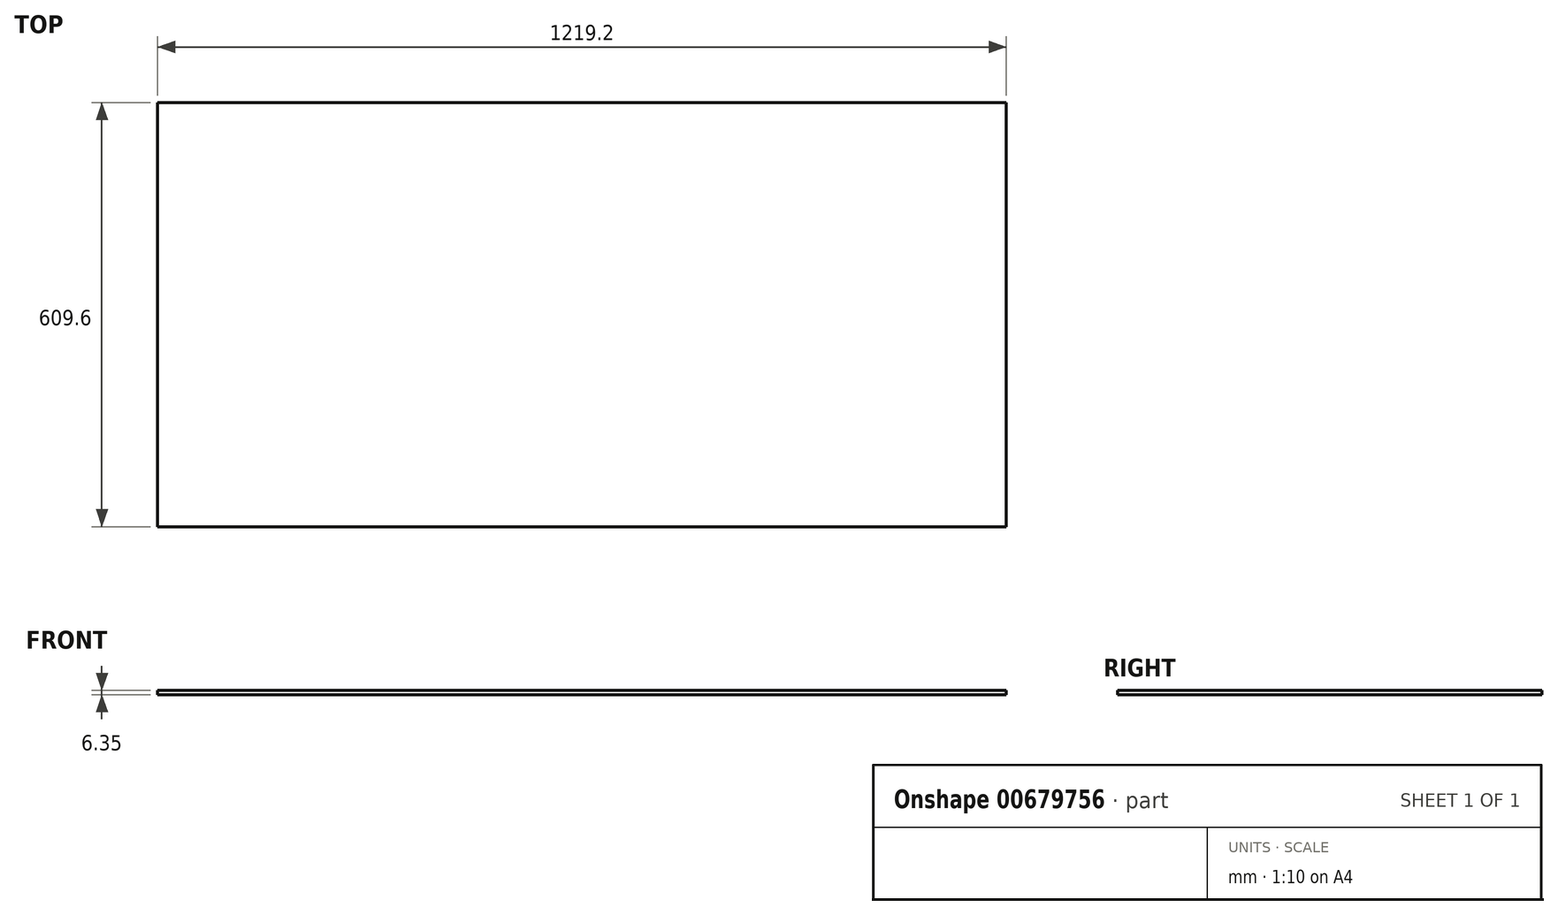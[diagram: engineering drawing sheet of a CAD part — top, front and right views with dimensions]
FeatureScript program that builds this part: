
annotation { "Feature Type Name" : "Feature", "Feature Type Description" : "" }
export const myFeature = defineFeature(function(context is Context, id is Id, definition is map)
    precondition{}
    {
        {
            var Q0;
            Q0=qCreatedBy(makeId("Top.planeOp"),FACE);
            var sketch = newSketch(context, id + "F0", { "sketchPlane" : qUnion([Q0])});
            skLineSegment(sketch, "E0.bottom", {"start": v(609.6, -304.8) * mm, "end": v(-609.6, -304.8) * mm});
            skLineSegment(sketch, "E0.top", {"start": v(609.6, 304.8) * mm, "end": v(-609.6, 304.8) * mm});
            skLineSegment(sketch, "E0.left", {"start": v(609.6, -304.8) * mm, "end": v(609.6, 304.8) * mm});
            skLineSegment(sketch, "E0.right", {"start": v(-609.6, -304.8) * mm, "end": v(-609.6, 304.8) * mm});
            skPoint(sketch, "E0.middle", {"position": v(0, 0) * mm});
            skSolve(sketch);
        }
        {
            var Q0;
            Q0 = qSketchRegion(id + "F0", true);
            extrude(context, id + "F1", {"entities" : qUnion([Q0]), "depth" : 6.35 * mm, "offsetDistance" : 30.48 * mm});
        }
    });
